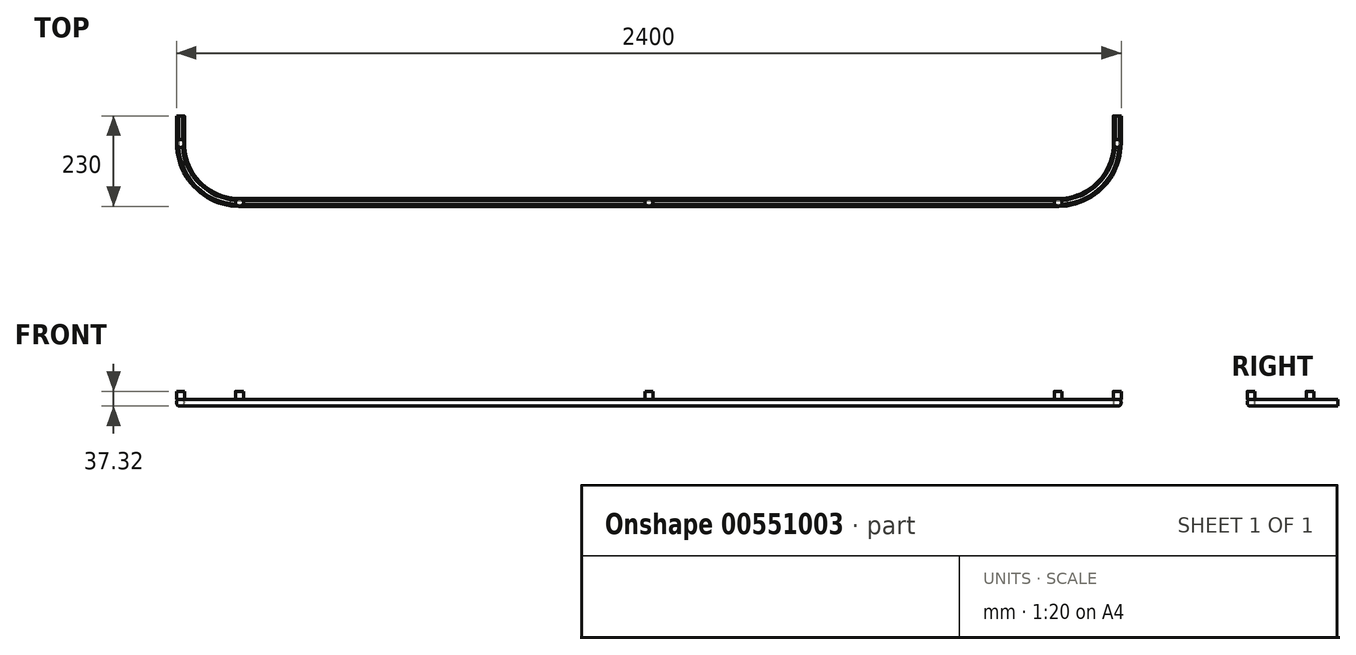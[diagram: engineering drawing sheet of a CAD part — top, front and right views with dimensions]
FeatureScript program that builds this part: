
annotation { "Feature Type Name" : "Feature", "Feature Type Description" : "" }
export const myFeature = defineFeature(function(context is Context, id is Id, definition is map)
    precondition{}
    {
        {
            var Q0;
            Q0=qCreatedBy(makeId("Front.planeOp"),FACE);
            var sketch = newSketch(context, id + "F0", { "sketchPlane" : qUnion([Q0])});
            skArc(sketch, "E0", {"start": v(-5, 8.66) * mm, "mid": v(-10, 0) * mm, "end": v(-5, -8.66) * mm});
            skLineSegment(sketch, "E1", {"start": v(-5, 8.66) * mm, "end": v(5, 8.66) * mm});
            skLineSegment(sketch, "E2", {"start": v(0, 0) * mm, "end": v(0, 10) * mm});
            skPoint(sketch, "E2.endSnap0", {"position": v(0, 8.66) * mm});
            skLineSegment(sketch, "E3", {"start": v(-5, -8.66) * mm, "end": v(5, -8.66) * mm});
            skArc(sketch, "E4.trimOffspring", {"start": v(5, -8.66) * mm, "mid": v(10, 0) * mm, "end": v(5, 8.66) * mm});
            skSolve(sketch);
        }
        {
            var Q0;
            Q0=qCreatedBy(makeId("Top.planeOp"),FACE);
            var sketch = newSketch(context, id + "F1", { "sketchPlane" : qUnion([Q0])});
            skLineSegment(sketch, "E5", {"start": v(0, 0) * mm, "end": v(0, -70) * mm});
            skLineSegment(sketch, "E6", {"start": v(150, -220) * mm, "end": v(2230, -220) * mm});
            skLineSegment(sketch, "E7", {"start": v(2380, -70) * mm, "end": v(2380, 0) * mm});
            skPoint(sketch, "E8.visualSharp", {"position": v(0, -220) * mm});
            skArc(sketch, "E8.filletArc", {"start": v(0, -70) * mm, "mid": v(43.93, -176.07) * mm, "end": v(150, -220) * mm});
            skPoint(sketch, "E9.visualSharp", {"position": v(2380, -220) * mm});
            skArc(sketch, "E9.filletArc", {"start": v(2230, -220) * mm, "mid": v(2336.07, -176.07) * mm, "end": v(2380, -70) * mm});
            skSolve(sketch);
        }
        {
            var Q0;
            {var subQ0=sQuery(id+"F0.wireOp",EDGE,"E0");Q0=makeQuery(id+"F0.imprint","IMPRINT",FACE,{"disambiguationData":[TD([[makeQuery(id+"F0.imprint","IMPRINT",EDGE,{"derivedFrom":subQ0}),1.0]])]});}
            var Q1;
            Q1=sQuery(id+"F1.wireOp",EDGE,"E5");
            var Q2;
            Q2=sQuery(id+"F1.wireOp",EDGE,"E8.filletArc");
            var Q3;
            Q3=sQuery(id+"F1.wireOp",EDGE,"E6");
            var Q4;
            Q4=sQuery(id+"F1.wireOp",EDGE,"E9.filletArc");
            var Q5;
            Q5=sQuery(id+"F1.wireOp",EDGE,"E7");
            sweep(context, id + "F2", {"profiles" : qUnion([Q0]), "path" : qUnion([Q1, Q2, Q3, Q4, Q5])});
        }
        {
            var Q0;
            Q0=makeQuery(id+"F2.opSweep","SWEPT_FACE",FACE,{"disambiguationData":[OSD([sQuery(id+"F0.wireOp",EDGE,"E1"),sQuery(id+"F1.wireOp",EDGE,"E5")])]});
            var sketch = newSketch(context, id + "F3", { "sketchPlane" : qUnion([Q0])});
            skCircle(sketch, "E10", {"center": v(0, -70) * mm, "radius": 10 * mm});
            skCircle(sketch, "E11", {"center": v(150, -220) * mm, "radius": 10 * mm});
            skLineSegment(sketch, "E12", {"start": v(1190, -215) * mm, "end": v(1190, -225) * mm});
            skCircle(sketch, "E13.MirrorC", {"center": v(2380, -70) * mm, "radius": 10 * mm});
            skCircle(sketch, "E14.MirrorC", {"center": v(2230, -220) * mm, "radius": 10 * mm});
            skSolve(sketch);
        }
        {
            var Q0;
            Q0 = qSketchRegion(id + "F3", true);
            extrude(context, id + "F4", {"entities" : qUnion([Q0]), "operationType" : NewBodyOperationType.ADD, "depth" : 20 * mm, "offsetDistance" : 25 * mm});
        }
        {
            var Q0;
            {var subQ1=sQuery(id+"F1.wireOp",EDGE,"E6");Q0=makeQuery(id+"F4.boolean.opBoolean","SPLIT",FACE,{"disambiguationData":[TD([makeQuery(id+"F2.opSweep","SWEPT_FACE",FACE,{"disambiguationData":[OSD([sQuery(id+"F0.wireOp",EDGE,"E0"),subQ1])]})])],"derivedFrom":makeQuery(id+"F2.opSweep","SWEPT_FACE",FACE,{"disambiguationData":[OSD([sQuery(id+"F0.wireOp",EDGE,"E1"),sQuery(id+"F1.wireOp",EDGE,"E5")])]})});}
            var sketch = newSketch(context, id + "F5", { "sketchPlane" : qUnion([Q0])});
            skLineSegment(sketch, "E15", {"start": v(1190, -215) * mm, "end": v(1190, -225) * mm});
            skLineSegment(sketch, "E16", {"start": v(1190, -220) * mm, "end": v(150, -220) * mm});
            skCircle(sketch, "E17", {"center": v(843.3, -220) * mm, "radius": 10 * mm});
            skCircle(sketch, "E18", {"center": v(1536.6, -220) * mm, "radius": 10 * mm});
            skCircle(sketch, "E19", {"center": v(1190, -220) * mm, "radius": 10 * mm});
            skSolve(sketch);
        }
        {
            var Q0;
            {var subQ0=sQuery(id+"F5.wireOp",EDGE,"E19");var subQ1=sQuery(id+"F0.wireOp",EDGE,"E1");var subQ2=sQuery(id+"F1.wireOp",EDGE,"E6");var subQ3=sQuery(id+"F0.wireOp",EDGE,"E4.trimOffspring");var subQ4=makeQuery(id+"F4.boolean.opBoolean","SPLIT",EDGE,{"disambiguationData":[topologyDisambiguationEdgeConnected([makeQuery(id+"F2.opSweep","SWEPT_FACE",FACE,{"disambiguationData":[OSD([subQ1,sQuery(id+"F1.wireOp",EDGE,"E5")])]})])],"derivedFrom":makeQuery(id+"F2.opSweep","SWEPT_EDGE",EDGE,{"disambiguationData":[OSD([subQ1,subQ3,subQ2])]})});var subQ5=makeQuery(id+"F5.imprint","INTERSECT",VERTEX,{"disambiguationData":[OD(0.0)],"derivedFrom":[subQ4,subQ0]});Q0=makeQuery(id+"F5.imprint","IMPRINT",FACE,{"disambiguationData":[TD([[makeQuery(id+"F5.imprint","IMPRINT",EDGE,{"disambiguationData":[TD([[subQ5,1.0]])],"derivedFrom":subQ0}),1.0]])]});}
            var Q1;
            {var subQ0=sQuery(id+"F5.wireOp",EDGE,"E15");var subQ9=makeQuery(id+"F5.imprint","INTERSECT",VERTEX,{"derivedFrom":[subQ0,sQuery(id+"F5.wireOp",EDGE,"E16")]});Q1=makeQuery(id+"F5.imprint","IMPRINT",FACE,{"disambiguationData":[TD([[makeQuery(id+"F5.imprint","IMPRINT",EDGE,{"disambiguationData":[TD([[subQ9,1.0]])],"derivedFrom":subQ0}),1.0]])]});}
            var Q2;
            {var subQ0=sQuery(id+"F5.wireOp",EDGE,"E15");var subQ6=sQuery(id+"F5.wireOp",EDGE,"E16");var subQ7=makeQuery(id+"F5.imprint","INTERSECT",VERTEX,{"derivedFrom":[subQ0,subQ6]});Q2=makeQuery(id+"F5.imprint","IMPRINT",FACE,{"disambiguationData":[TD([[makeQuery(id+"F5.imprint","IMPRINT",EDGE,{"disambiguationData":[TD([[subQ7,-1.0]])],"derivedFrom":subQ6}),1.0]])]});}
            var Q3;
            {var subQ0=sQuery(id+"F5.wireOp",EDGE,"E15");var subQ6=sQuery(id+"F5.wireOp",EDGE,"E16");var subQ7=makeQuery(id+"F5.imprint","INTERSECT",VERTEX,{"derivedFrom":[subQ0,subQ6]});Q3=makeQuery(id+"F5.imprint","IMPRINT",FACE,{"disambiguationData":[TD([[makeQuery(id+"F5.imprint","IMPRINT",EDGE,{"disambiguationData":[TD([[subQ7,-1.0]])],"derivedFrom":subQ6}),-1.0]])]});}
            var Q4;
            {var subQ0=sQuery(id+"F5.wireOp",EDGE,"E19");var subQ1=sQuery(id+"F1.wireOp",EDGE,"E6");var subQ2=sQuery(id+"F0.wireOp",EDGE,"E0");var subQ3=sQuery(id+"F0.wireOp",EDGE,"E1");var subQ4=makeQuery(id+"F4.boolean.opBoolean","SPLIT",EDGE,{"disambiguationData":[topologyDisambiguationEdgeConnected([makeQuery(id+"F2.opSweep","SWEPT_FACE",FACE,{"disambiguationData":[OSD([subQ3,sQuery(id+"F1.wireOp",EDGE,"E5")])]})])],"derivedFrom":makeQuery(id+"F2.opSweep","SWEPT_EDGE",EDGE,{"disambiguationData":[OSD([subQ2,subQ3,subQ1])]})});var subQ5=makeQuery(id+"F5.imprint","INTERSECT",VERTEX,{"disambiguationData":[OD(0.0)],"derivedFrom":[subQ4,subQ0]});Q4=makeQuery(id+"F5.imprint","IMPRINT",FACE,{"disambiguationData":[TD([[makeQuery(id+"F5.imprint","IMPRINT",EDGE,{"disambiguationData":[TD([[subQ5,-1.0]])],"derivedFrom":subQ0}),1.0]])]});}
            var Q5;
            Q5=sQuery(id+"F5.wireOp",EDGE,"E19");
            extrude(context, id + "F6", {"entities" : qUnion([Q0, Q1, Q2, Q3, Q4]), "operationType" : NewBodyOperationType.ADD, "surfaceEntities" : qUnion([Q5]), "depth" : 20 * mm, "offsetDistance" : 25 * mm});
        }
    });
